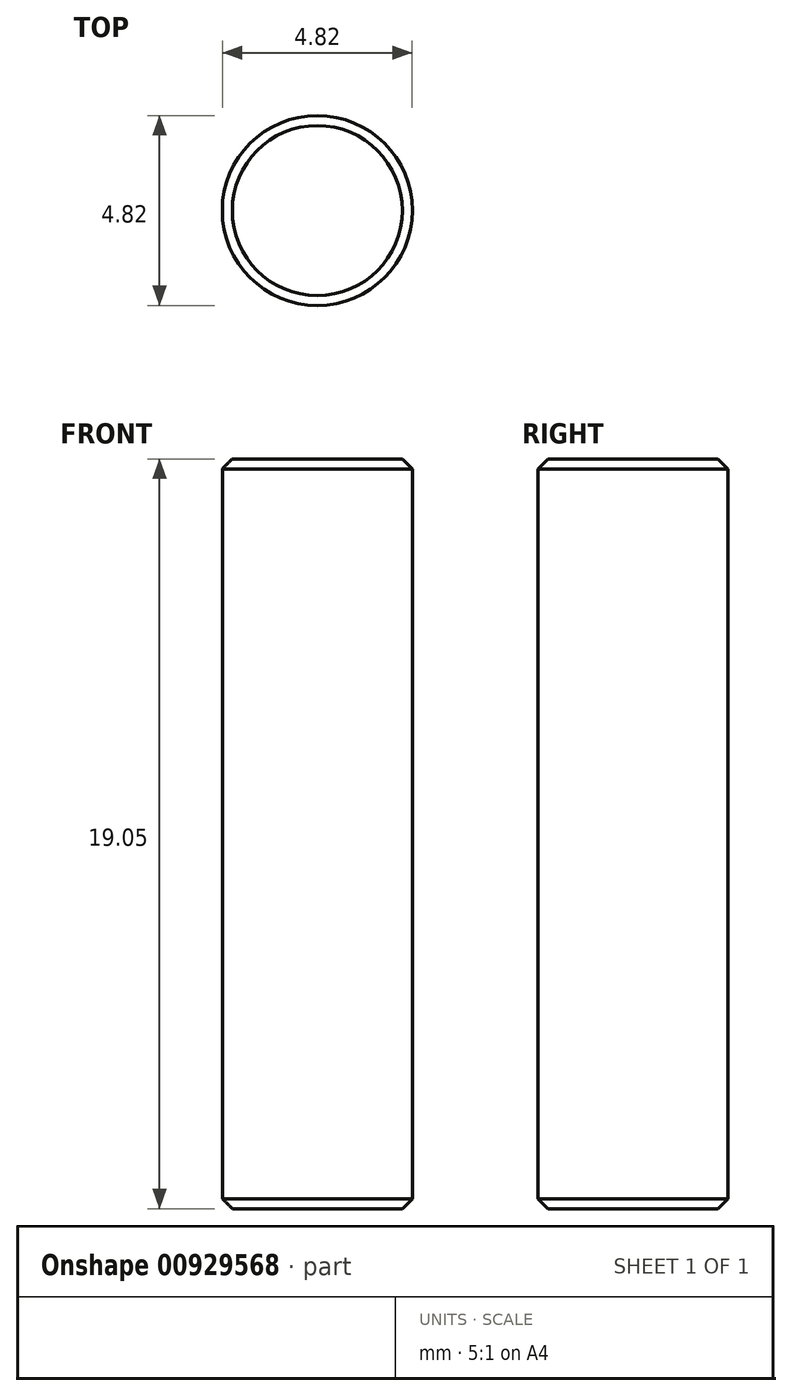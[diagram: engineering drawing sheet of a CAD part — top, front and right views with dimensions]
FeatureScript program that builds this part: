
annotation { "Feature Type Name" : "Feature", "Feature Type Description" : "" }
export const myFeature = defineFeature(function(context is Context, id is Id, definition is map)
    precondition{}
    {
        {
            var Q0;
            Q0=qCreatedBy(makeId("Right.planeOp"),FACE);
            var sketch = newSketch(context, id + "F0", { "sketchPlane" : qUnion([Q0])});
            skLineSegment(sketch, "E0.bottom", {"start": v(0, 0) * mm, "end": v(2.41, 0) * mm});
            skLineSegment(sketch, "E0.top", {"start": v(0, 19.05) * mm, "end": v(2.41, 19.05) * mm});
            skLineSegment(sketch, "E0.left", {"start": v(0, 0) * mm, "end": v(0, 19.05) * mm});
            skLineSegment(sketch, "E0.right", {"start": v(2.41, 0) * mm, "end": v(2.41, 19.05) * mm});
            skSolve(sketch);
        }
        {
            var Q0;
            Q0 = qSketchRegion(id + "F0", true);
            var Q1;
            Q1=sQuery(id+"F0.wireOp",EDGE,"E0.left");
            revolve(context, id + "F1", {"surfaceOperationType" : NewSurfaceOperationType.NEW, "entities" : qUnion([Q0]), "axis" : qUnion([Q1]), "revolveType" : RevolveType.FULL});
        }
        {
            var Q0;
            Q0=makeQuery(id+"F1.opRevolve","SWEPT_EDGE",EDGE,{"disambiguationData":[OSD([sQuery(id+"F0.wireOp",EDGE,"E0.top"),sQuery(id+"F0.wireOp",EDGE,"E0.right")])]});
            var Q1;
            Q1=makeQuery(id+"F1.opRevolve","SWEPT_EDGE",EDGE,{"disambiguationData":[OSD([sQuery(id+"F0.wireOp",EDGE,"E0.bottom"),sQuery(id+"F0.wireOp",EDGE,"E0.right")])]});
            chamfer(context, id + "F2", {"entities" : qUnion([Q0, Q1]), "width" : 0.25 * mm, "tangentPropagation" : true});
        }
    });
